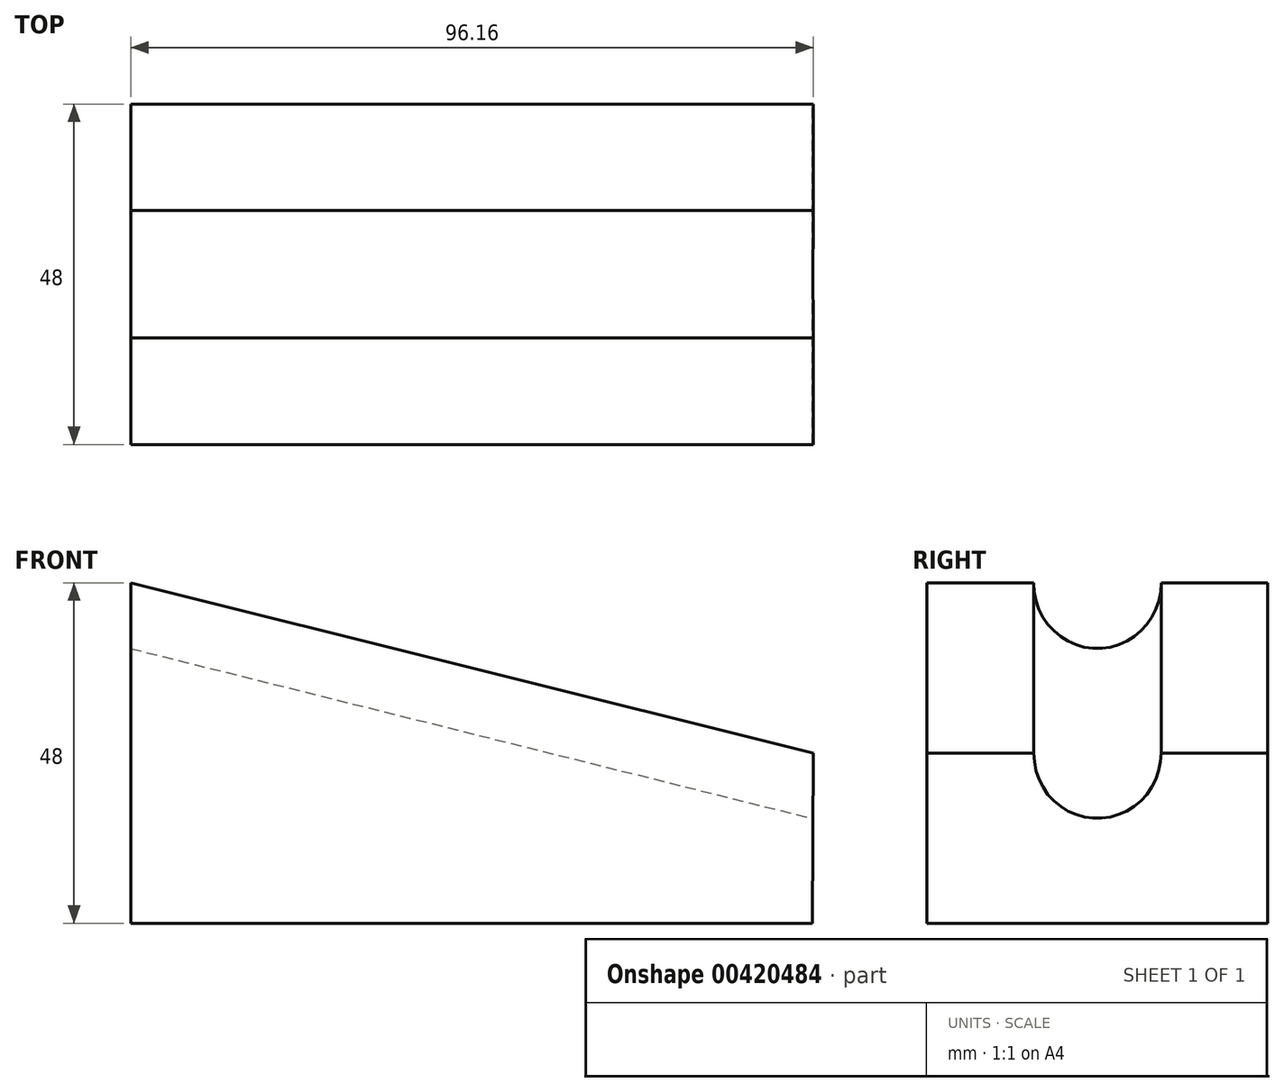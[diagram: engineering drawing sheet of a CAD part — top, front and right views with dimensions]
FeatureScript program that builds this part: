
annotation { "Feature Type Name" : "Feature", "Feature Type Description" : "" }
export const myFeature = defineFeature(function(context is Context, id is Id, definition is map)
    precondition{}
    {
        {
            var Q0;
            Q0=qCreatedBy(makeId("Front.planeOp"),FACE);
            var sketch = newSketch(context, id + "F0", { "sketchPlane" : qUnion([Q0])});
            skLineSegment(sketch, "E0", {"start": v(-28.54, 0) * mm, "end": v(67.46, 0) * mm});
            skLineSegment(sketch, "E1", {"start": v(-28.54, 0) * mm, "end": v(-28.54, 48) * mm});
            skLineSegment(sketch, "E2", {"start": v(-28.54, 48) * mm, "end": v(67.62, 24) * mm});
            skLineSegment(sketch, "E3", {"start": v(67.62, 24) * mm, "end": v(67.46, 0) * mm});
            skSolve(sketch);
        }
        {
            var Q0;
            Q0=makeQuery(id+"F0.imprint","IMPRINT",FACE,{"disambiguationData":[TD([[makeQuery(id+"F0.imprint","IMPRINT",EDGE,{"derivedFrom":sQuery(id+"F0.wireOp",EDGE,"E0")}),1.0]])]});
            extrude(context, id + "F1", {"entities" : qUnion([Q0]), "depth" : 48 * mm, "symmetric" : true});
        }
        {
            var Q0;
            Q0=makeQuery(id+"F1.opExtrude","SWEPT_FACE",FACE,{"disambiguationData":[OSD([sQuery(id+"F0.wireOp",EDGE,"E2")])]});
            var sketch = newSketch(context, id + "F2", { "sketchPlane" : qUnion([Q0])});
            skLineSegment(sketch, "E4.bottom", {"start": v(-39.32, 0) * mm, "end": v(65.12, 0) * mm});
            skLineSegment(sketch, "E4.top", {"start": v(-39.32, 9) * mm, "end": v(65.12, 9) * mm});
            skLineSegment(sketch, "E4.left", {"start": v(-39.32, 0) * mm, "end": v(-39.32, 9) * mm});
            skLineSegment(sketch, "E4.right", {"start": v(65.12, 0) * mm, "end": v(65.12, 9) * mm});
            skSolve(sketch);
        }
        {
            var Q0;
            {var subQ0=sQuery(id+"F2.wireOp",EDGE,"E4.left");Q0=makeQuery(id+"F2.imprint","IMPRINT",FACE,{"disambiguationData":[TD([[makeQuery(id+"F2.imprint","IMPRINT",EDGE,{"derivedFrom":subQ0}),-1.0]])]});}
            var Q1;
            {var subQ0=sQuery(id+"F2.wireOp",EDGE,"E4.right");Q1=makeQuery(id+"F2.imprint","IMPRINT",FACE,{"disambiguationData":[TD([[makeQuery(id+"F2.imprint","IMPRINT",EDGE,{"derivedFrom":subQ0}),1.0]])]});}
            var Q2;
            Q2=sQuery(id+"F2.wireOp",EDGE,"ZrMcM5Rx-0CaW-or26-815I-FCymAHvhAclH");
            var Q3;
            Q3=sQuery(id+"F2.wireOp",EDGE,"E4.bottom");
            revolve(context, id + "F3", {"operationType" : NewBodyOperationType.REMOVE, "entities" : qUnion([Q0, Q1]), "surfaceEntities" : qUnion([Q2]), "axis" : qUnion([Q3]), "revolveType" : RevolveType.FULL, "oppositeDirection" : true});
        }
    });
